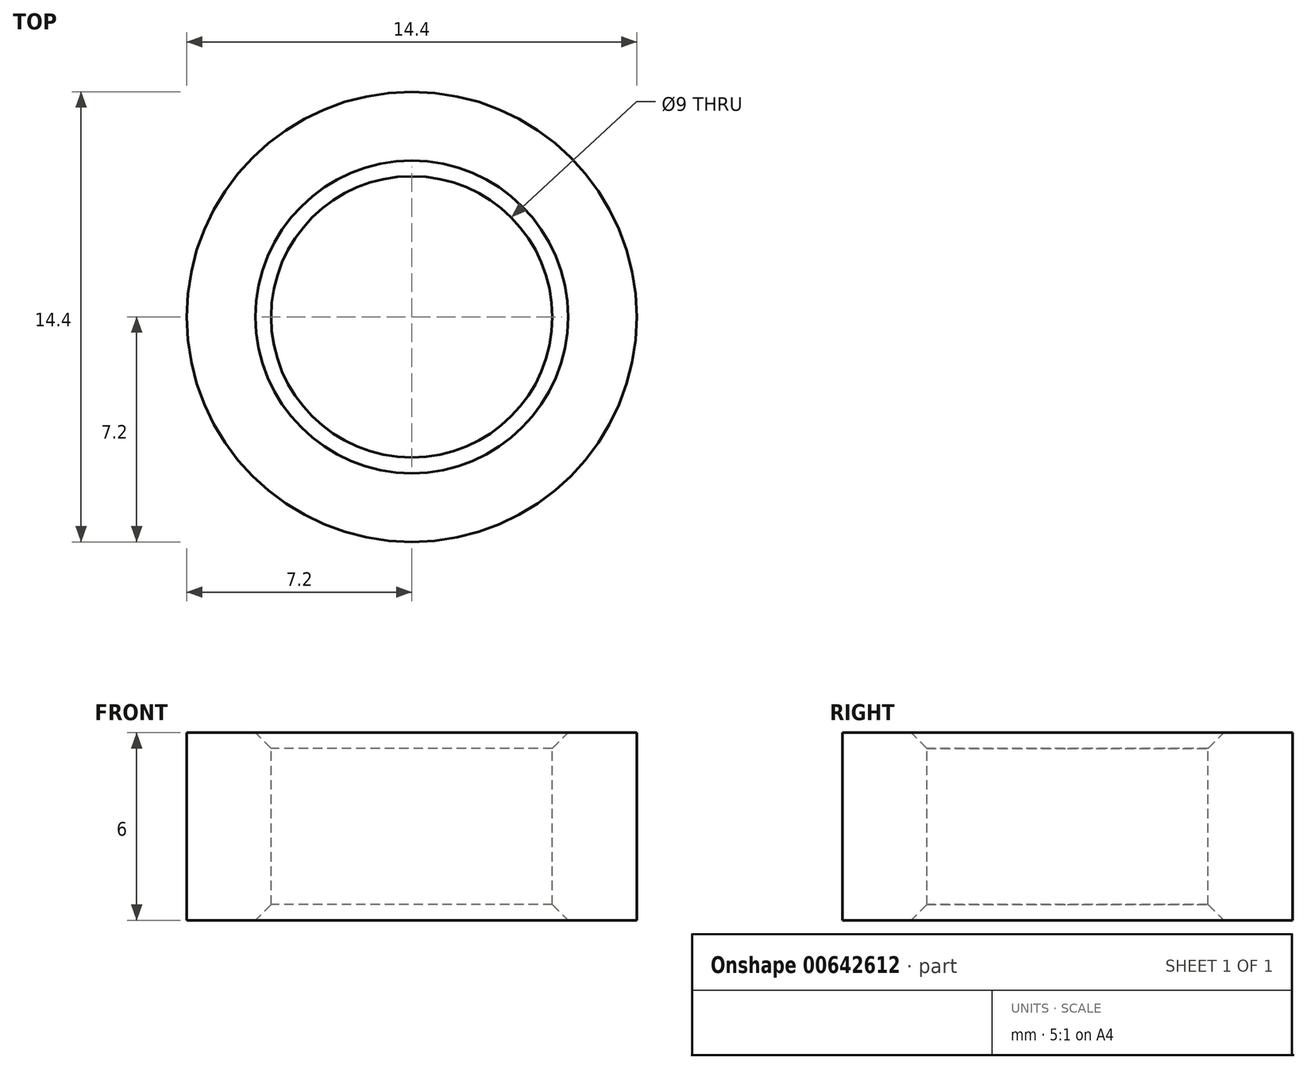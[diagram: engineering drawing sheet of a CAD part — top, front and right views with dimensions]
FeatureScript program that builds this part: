
annotation { "Feature Type Name" : "Feature", "Feature Type Description" : "" }
export const myFeature = defineFeature(function(context is Context, id is Id, definition is map)
    precondition{}
    {
        {
            var Q0;
            Q0=qCreatedBy(makeId("Top.planeOp"),FACE);
            var sketch = newSketch(context, id + "F0", { "sketchPlane" : qUnion([Q0])});
            skCircle(sketch, "E0", {"center": v(0, 0) * mm, "radius": 7.2 * mm});
            skSolve(sketch);
        }
        {
            var Q0;
            Q0 = qSketchRegion(id + "F0", true);
            extrude(context, id + "F1", {"entities" : qUnion([Q0]), "depth" : 6 * mm, "offsetDistance" : 25 * mm});
        }
        {
            var Q0;
            Q0=makeQuery(id+"F1.opExtrude","CAP_FACE",FACE,{"disambiguationData":[OSD([sQuery(id+"F0.wireOp",EDGE,"E0")])],"isStart":false});
            var sketch = newSketch(context, id + "F2", { "sketchPlane" : qUnion([Q0])});
            skCircle(sketch, "E1", {"center": v(0, 0) * mm, "radius": 4.5 * mm});
            skSolve(sketch);
        }
        {
            var Q0;
            Q0=makeQuery(id+"F2.imprint","IMPRINT",FACE,{"disambiguationData":[TD([[makeQuery(id+"F2.imprint","IMPRINT",EDGE,{"derivedFrom":sQuery(id+"F2.wireOp",EDGE,"E1")}),1.0]])]});
            extrude(context, id + "F3", {"entities" : qUnion([Q0]), "operationType" : NewBodyOperationType.REMOVE, "endBound" : BoundingType.THROUGH_ALL, "oppositeDirection" : true, "depth" : 6 * mm, "offsetDistance" : 25 * mm});
        }
        {
            var Q0;
            Q0=makeQuery(id+"F3.boolean.opBoolean","COPY",FACE,{"derivedFrom":makeQuery(id+"F3.opExtrude","SWEPT_FACE",FACE,{"disambiguationData":[OSD([sQuery(id+"F2.wireOp",EDGE,"E1")])]})});
            chamfer(context, id + "F4", {"entities" : qUnion([Q0]), "chamferType" : ChamferType.OFFSET_ANGLE, "width" : 0.5 * mm, "oppositeDirection" : true, "angle" : 45 * degree, "tangentPropagation" : true});
        }
    });
